# Revit family: DG1012MRW
name_source: partatom
category: Lighting Fixtures
revit_build: Autodesk Revit 2017 (Build: 20160225_1515(x64)
units: mm (PartAtom-declared; Revit-internal decimal feet)

## family parameters
Cut with Voids When Loaded = No
Host = Face
Light Source = Yes
Part Type = Normal
Room Calculation Point = No
Round Connector Dimension = Use Diameter
Shared = No

## types (19) — shared parameters
Color Filter = 16777215
Default Elevation = 1219 mm
Dimming Lamp Color Temperature Shift = <None>
Emit Shape Visible in Rendering = Yes
Emit from Circle Diameter = 79 mm
Lamp = LED
Manufacturer = ARLIGHT
Model = DG1012MRW
Tilt Angle = 90.00°
Type Comments = DOWNLIGHT
Type Image = <None>

## per-type parameters (varying)
| type | Apparent Load | Description | Photometric Web File | Reflector Angle | Wattage Comments |
| DGMRW.120.10.30.65 | 9 VA | 19° | dg-1012-mrw-10w-4k-19drc.ies | 65° | 10 |
| DGMRW.120.10.40.30 | 9 VA | 30° | dg-1012-mrw-10w-4k-30drc.ies | 30° | 10 |
| DGMRW.120.10.30.75 | 9 VA | 75° | dg-1012-mrw-10w-4k-75drc.ies | 75° | 10 |
| DGMRW.120.14.40.75 | 13 VA | 75° | dg-1012-mrw-14w-4k-75drc.ies | 75° | 14 |
| DGMRW.120.14.40.30 | 13 VA | 30° | dg-1012-mrw-14w-4k-30drc.ies | 30° | 14 |
| DGMRW.120.14.40.19 | 13 VA | 19° | dg-1012-mrw-14w-4k-19drc.ies | 19° | 14 |
| DGMRW.120.20.40.19 | 20 VA | 19° | dg-1012-mrw-20w-4k-19drc.ies | 19° | 20 |
| DGMRW.120.20.40.30 | 20 VA | 30° | dg-1012-mrw-20w-4k-30drc.ies | 30° | 20 |
| DGMRW.120.20.40.75 | 20 VA | 75° | dg-1012-mrw-20w-4k-75drc.ies | 75° | 20 |
| DGMRW.120.14.30.19 | 14 VA | 75° | dg-1012-mrw-10w-4k-75drc.ies | 19° | 14W |
| DGMRW.120.14.30.30 | 13 VA | 19° | dg-1012-mrw-14w-4k-19drc.ies | 30° | 14 |
| DGMRW.120.14.40.65 | 13 VA | 19° | dg-1012-mrw-14w-4k-19drc.ies | 65° | 14 |
| DGMRW.120.14.30.65 | 13 VA | 19° | dg-1012-mrw-14w-4k-19drc.ies | 65° | 14 |
| DGMRW.120.14.30.75 | 13 VA | 19° | dg-1012-mrw-14w-4k-19drc.ies | 75° | 14 |
| DGMRW.120.20.30.19 | 20 VA | 19° | dg-1012-mrw-14w-4k-19drc.ies | 19° | 20W |
| DGMRW.120.20.30.30 | 20 VA | 19° | dg-1012-mrw-14w-4k-19drc.ies | 30° | 20W |
| DGMRW.120.20.40.65 | 20 VA | 30° | dg-1012-mrw-20w-4k-30drc.ies | 65° | 20 |
| DGMRW.120.20.30.65 | 20 VA | 30° | dg-1012-mrw-20w-4k-30drc.ies | 65° | 20W |
| DGMRW.120.20.30.75 | 20 VA | 75° | dg-1012-mrw-20w-4k-75drc.ies | 75° | 20 |

## geometry (parser evidence)
native form markers: Sweep x2
no freeform markers — native parametric forms only
